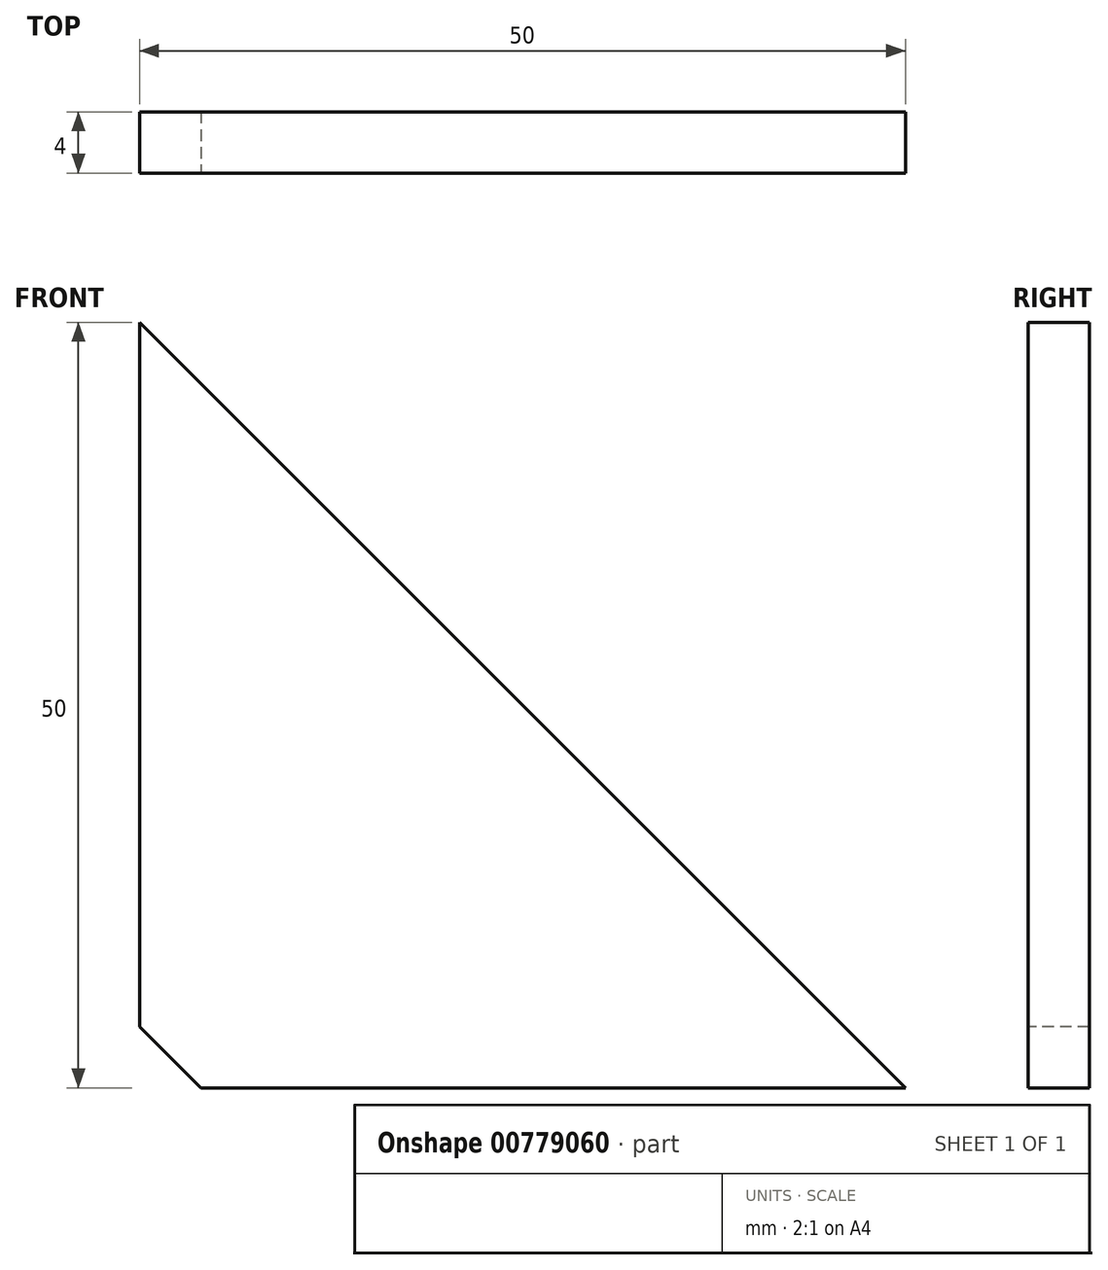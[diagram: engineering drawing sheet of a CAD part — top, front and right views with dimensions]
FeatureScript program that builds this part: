
annotation { "Feature Type Name" : "Feature", "Feature Type Description" : "" }
export const myFeature = defineFeature(function(context is Context, id is Id, definition is map)
    precondition{}
    {
        {
            var Q0;
            Q0=qCreatedBy(makeId("Front.planeOp"),FACE);
            var sketch = newSketch(context, id + "F0", { "sketchPlane" : qUnion([Q0])});
            skLineSegment(sketch, "E0", {"start": v(0, 0) * mm, "end": v(0, 50) * mm});
            skLineSegment(sketch, "E1", {"start": v(0, 0) * mm, "end": v(50, 0) * mm});
            skLineSegment(sketch, "E2", {"start": v(50, 0) * mm, "end": v(0, 50) * mm});
            skLineSegment(sketch, "E3", {"start": v(0, 0) * mm, "end": v(0, 80) * mm});
            skLineSegment(sketch, "E4", {"start": v(0, 0) * mm, "end": v(0, 4) * mm});
            skLineSegment(sketch, "E5", {"start": v(0, 4) * mm, "end": v(4, 0) * mm});
            skSolve(sketch);
        }
        {
            var Q0;
            {var subQ0=sQuery(id+"F0.wireOp",EDGE,"E2");Q0=makeQuery(id+"F0.imprint","IMPRINT",FACE,{"disambiguationData":[TD([[makeQuery(id+"F0.imprint","IMPRINT",EDGE,{"derivedFrom":subQ0}),1.0]])]});}
            extrude(context, id + "F1", {"entities" : qUnion([Q0]), "oppositeDirection" : true, "depth" : 4 * mm, "offsetDistance" : 25 * mm});
        }
    });
